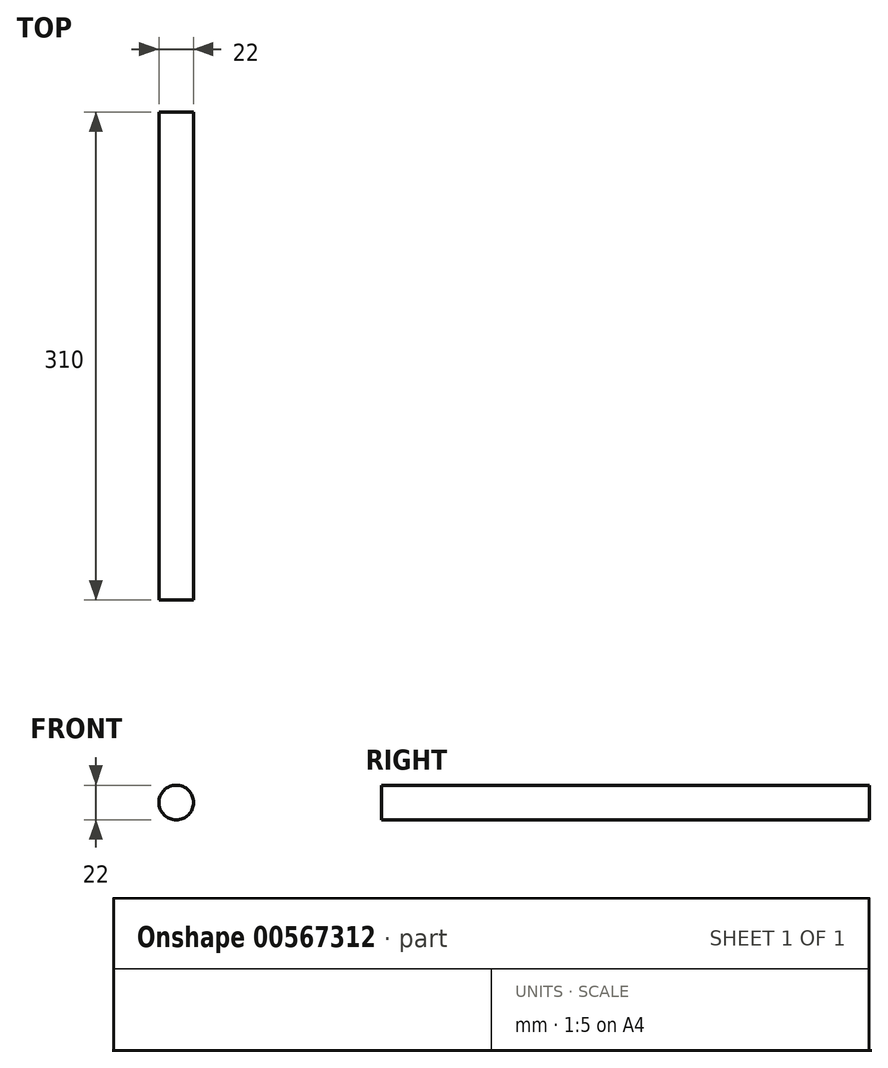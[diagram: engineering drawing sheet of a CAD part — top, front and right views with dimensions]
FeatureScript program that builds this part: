
annotation { "Feature Type Name" : "Feature", "Feature Type Description" : "" }
export const myFeature = defineFeature(function(context is Context, id is Id, definition is map)
    precondition{}
    {
        {
            var Q0;
            Q0=qCreatedBy(makeId("Front.planeOp"),FACE);
            var sketch = newSketch(context, id + "F0", { "sketchPlane" : qUnion([Q0])});
            skCircle(sketch, "E0", {"center": v(0, 0) * mm, "radius": 11 * mm});
            skSolve(sketch);
        }
        {
            var Q0;
            Q0 = qSketchRegion(id + "F0", true);
            extrude(context, id + "F1", {"entities" : qUnion([Q0]), "depth" : 310 * mm, "offsetDistance" : 25 * mm});
        }
    });
